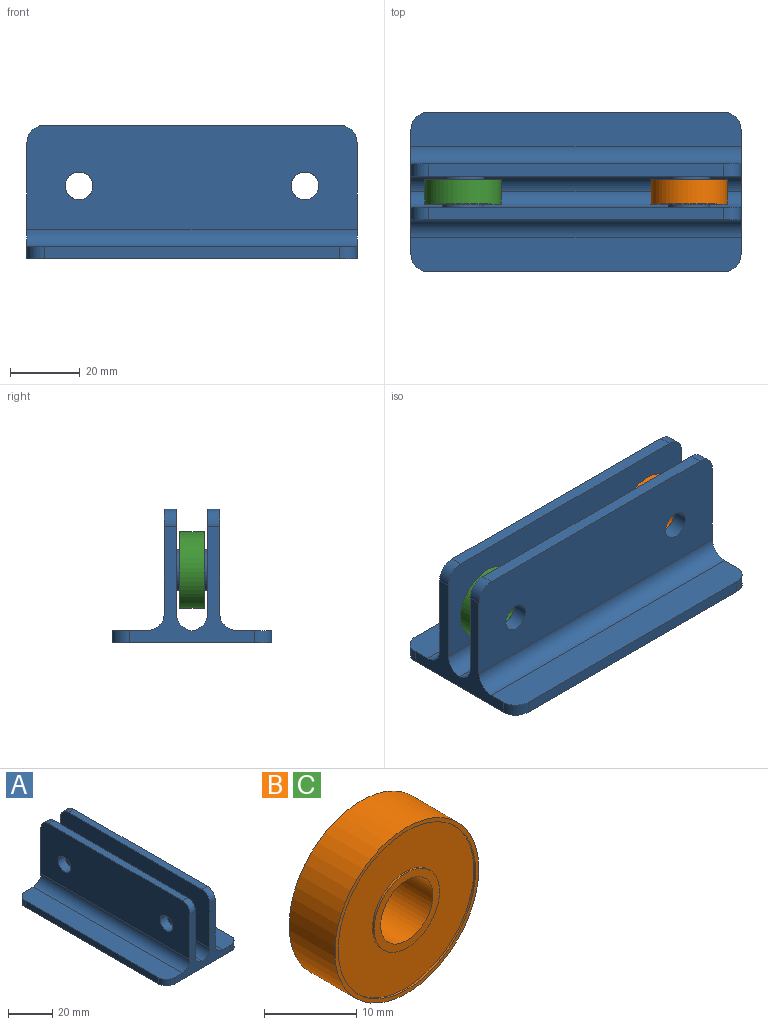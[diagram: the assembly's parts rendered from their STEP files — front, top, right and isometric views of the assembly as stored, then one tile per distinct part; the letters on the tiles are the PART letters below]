
ASSEMBLY  parts=3 mates=2
PART A: 37 faces, bbox 46x95x38.5 mm
  f0: plane 95x30mm, normal (1,0,0), area 2613.1mm2, adj f1,f6,f7,f8,f10,f26,f34,f36
  f1: plane 85x3.5mm, normal (0,0,1), area 297.5mm2, adj f0,f2,f34,f36
  f2: plane 95x30mm, normal (-1,0,0), area 2738.7mm2, adj f1,f6,f7,f12,f13,f32,f34,f36
  f3: plane 95x10mm, normal (0,0,1), area 939.3mm2, adj f4,f6,f7,f32,f33,f35
  f4: plane 85x3.5mm, normal (-1,0,0), area 297.5mm2, adj f3,f5,f33,f35
  f5: plane 95x46mm, normal (0,0,-1), area 4348.5mm2, adj f4,f6,f7,f18,f29,f31,f33,f35
  f6: plane 36x33.5mm, normal (0,-1,0), area 357.5mm2, adj f0,f2,f3,f5,f14,f16,f17,f25
  f7: plane 36x33.5mm, normal (0,1,0), area 357.5mm2, adj f0,f2,f3,f5,f14,f16,f17,f26
  f8: cylinder r=6mm len=12mm, axis (-1,0,0), area 37.7mm2, adj f0,f9
  f9: plane 12x12mm, normal (1,0,0), area 62.8mm2, adj f8,f12
  f10: cylinder r=6mm len=12mm, axis (-1,0,0), area 37.7mm2, adj f0,f11
  f11: plane 12x12mm, normal (1,0,0), area 62.8mm2, adj f10,f13
  f12: cylinder r=4mm len=8mm, axis (1,0,0), area 113.1mm2, adj f2,f9
  f13: cylinder r=4mm len=8mm, axis (1,0,0), area 113.1mm2, adj f2,f11
  f14: plane 95x30mm, normal (-1,0,0), area 2613.1mm2, adj f6,f7,f15,f19,f21,f25,f27,f30
  f15: plane 85x3.5mm, normal (0,0,1), area 297.5mm2, adj f14,f16,f25,f30
  f16: plane 95x30mm, normal (1,0,0), area 2738.7mm2, adj f6,f7,f15,f23,f24,f25,f28,f30
  f17: plane 95x10mm, normal (0,0,1), area 939.3mm2, adj f6,f7,f18,f28,f29,f31
  f18: plane 85x3.5mm, normal (1,0,0), area 297.5mm2, adj f5,f17,f29,f31
  f19: cylinder r=6mm len=12mm, axis (1,0,0), area 37.7mm2, adj f14,f20
  f20: plane 12x12mm, normal (-1,0,0), area 62.8mm2, adj f19,f23
  f21: cylinder r=6mm len=12mm, axis (1,0,0), area 37.7mm2, adj f14,f22
  f22: plane 12x12mm, normal (-1,0,0), area 62.8mm2, adj f21,f24
  f23: cylinder r=4mm len=8mm, axis (-1,0,0), area 113.1mm2, adj f16,f20
  f24: cylinder r=4mm len=8mm, axis (-1,0,0), area 113.1mm2, adj f16,f22
  f25: cylinder r=5mm len=5mm, axis (-1,0,0), area 27.5mm2, adj f6,f14,f15,f16
  f26: cylinder r=5mm len=95mm, axis (0,-1,0), area 698.5mm2, adj f0,f6,f7,f27
  f27: cylinder r=5mm len=95mm, axis (0,-1,0), area 698.5mm2, adj f6,f7,f14,f26
  f28: cylinder r=5mm len=95mm, axis (0,-1,0), area 746.1mm2, adj f6,f7,f16,f17
  f29: cylinder r=5mm len=5mm, axis (0,0,-1), area 27.5mm2, adj f5,f7,f17,f18
  f30: cylinder r=5mm len=5mm, axis (1,0,0), area 27.5mm2, adj f7,f14,f15,f16
  f31: cylinder r=5mm len=5mm, axis (0,0,1), area 27.5mm2, adj f5,f6,f17,f18
  f32: cylinder r=5mm len=95mm, axis (0,-1,0), area 746.1mm2, adj f2,f3,f6,f7
  f33: cylinder r=5mm len=5mm, axis (0,0,-1), area 27.5mm2, adj f3,f4,f5,f7
  f34: cylinder r=5mm len=5mm, axis (-1,0,0), area 27.5mm2, adj f0,f1,f2,f7
  f35: cylinder r=5mm len=5mm, axis (0,0,1), area 27.5mm2, adj f3,f4,f5,f6
  f36: cylinder r=5mm len=5mm, axis (1,0,0), area 27.5mm2, adj f0,f1,f2,f6
PART B: 12 faces, bbox 22x7x22 mm
  f0: cylinder r=5mm len=10mm, axis (0,1,0), area 7.9mm2, adj f4,f11
  f1: cylinder r=4mm len=8mm, axis (0,1,0), area 175.9mm2, adj f3,f4
  f2: cylinder r=5mm len=10mm, axis (0,1,0), area 7.9mm2, adj f3,f10
  f3: plane 10x10mm, normal (0,-1,0), area 28.3mm2, adj f1,f2
  f4: plane 10x10mm, normal (0,1,0), area 28.3mm2, adj f0,f1
  f5: cylinder r=10.5mm len=21mm, axis (0,1,0), area 16.5mm2, adj f9,f11
  f6: cylinder r=10.5mm len=21mm, axis (0,1,0), area 16.5mm2, adj f8,f10
  f7: cylinder r=11mm len=22mm, axis (0,1,0), area 483.8mm2, adj f8,f9
  f8: plane 22x22mm, normal (0,-1,0), area 33.8mm2, adj f6,f7
  f9: plane 22x22mm, normal (0,1,0), area 33.8mm2, adj f5,f7
  f10: plane 21x21mm, normal (0,-1,0), area 267.8mm2, adj f2,f6
  f11: plane 21x21mm, normal (0,1,0), area 267.8mm2, adj f0,f5
PART C: same geometry as B
PLACE A rot(axis=(0,0,1),90deg) t=(28.69,6.85,-7.79)mm
PLACE B rot(axis=(1,0,0),180deg) t=(61.19,6.85,13.21)mm
PLACE C rot(axis=(1,0,0),180deg) t=(-3.81,6.85,13.21)mm
MATE fastened B.f0 <-> A.f19  axis (0,1,0) through (61.19,10.35,13.21)mm
MATE fastened C.f0 <-> A.f21  axis (0,1,0) through (-3.81,10.35,13.21)mm
